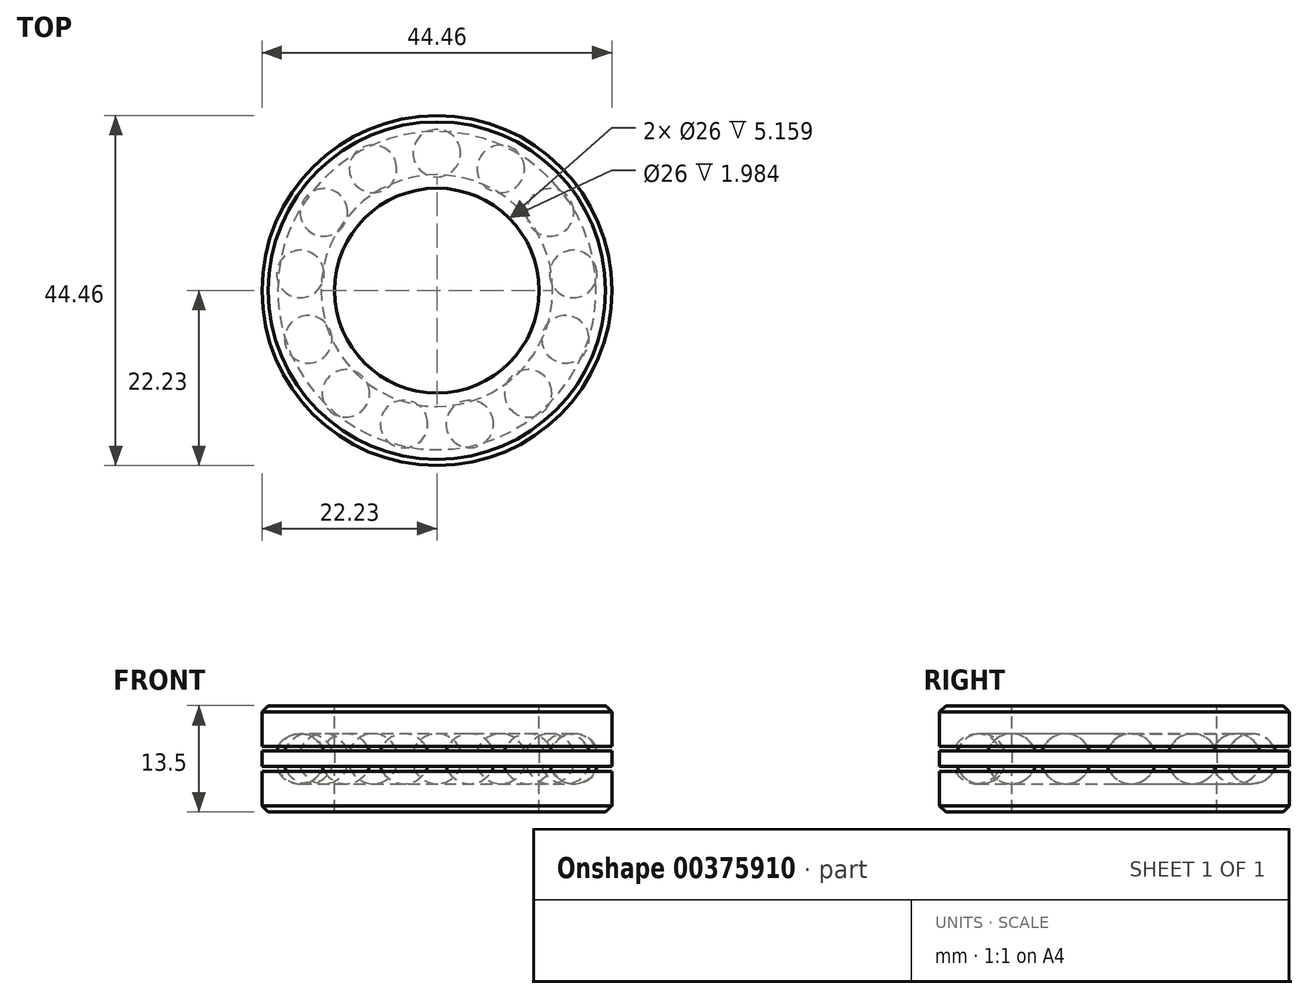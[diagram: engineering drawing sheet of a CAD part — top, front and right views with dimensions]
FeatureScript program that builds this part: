
annotation { "Feature Type Name" : "Feature", "Feature Type Description" : "" }
export const myFeature = defineFeature(function(context is Context, id is Id, definition is map)
    precondition{}
    {
        {
            var Q0;
            Q0=qCreatedBy(makeId("Top.planeOp"),FACE);
            var sketch = newSketch(context, id + "F0", { "sketchPlane" : qUnion([Q0]), "disableImprinting" : false});
            skCircle(sketch, "E0", {"center": v(0, 0) * mm, "radius": 17.46 * mm, "construction": true});
            skLineSegment(sketch, "E1", {"start": v(0, 0) * mm, "end": v(0, 34.15) * mm, "construction": true});
            skArc(sketch, "E2", {"start": v(0, 20.64) * mm, "mid": v(-3.17, 17.46) * mm, "end": v(0, 14.29) * mm});
            skLineSegment(sketch, "E3", {"start": v(0, 14.29) * mm, "end": v(0, 20.64) * mm});
            skCircle(sketch, "E4", {"center": v(0, 0) * mm, "radius": 13 * mm});
            skCircle(sketch, "E5", {"center": v(0, 0) * mm, "radius": 22.23 * mm});
            skSolve(sketch);
        }
        {
            var Q0;
            Q0=makeQuery(id+"F0.imprint","IMPRINT",FACE,{"disambiguationData":[TD([[makeQuery(id+"F0.imprint","IMPRINT",EDGE,{"derivedFrom":sQuery(id+"F0.wireOp",EDGE,"E2")}),1.0]])]});
            var Q1;
            Q1=sQuery(id+"F0.wireOp",EDGE,"E1");
            revolve(context, id + "F1", {"entities" : qUnion([Q0]), "axis" : qUnion([Q1]), "revolveType" : RevolveType.FULL});
        }
        {
            var Q0;
            Q0=makeQuery(id+"F0.imprint","IMPRINT",FACE,{"disambiguationData":[TD([[makeQuery(id+"F0.imprint","IMPRINT",EDGE,{"derivedFrom":sQuery(id+"F0.wireOp",EDGE,"E2")}),-1.0]])]});
            var Q1;
            Q1=makeQuery(id+"F0.imprint","IMPRINT",FACE,{"disambiguationData":[TD([[makeQuery(id+"F0.imprint","IMPRINT",EDGE,{"derivedFrom":sQuery(id+"F0.wireOp",EDGE,"E2")}),1.0]])]});
            extrude(context, id + "F2", {"entities" : qUnion([Q0, Q1]), "depth" : 1.98 * mm, "offsetDistance" : 25.4 * mm, "symmetric" : true});
        }
        {
            var Q0;
            Q0=makeQuery(id+"F1.opRevolve","SWEPT_BODY",BODY,{"disambiguationData":[OSD([sQuery(id+"F0.wireOp",EDGE,"E2"),sQuery(id+"F0.wireOp",EDGE,"E3")])]});
            var Q1;
            Q1=sQuery(id+"F0.wireOp",EDGE,"E0");
            circularPattern(context, id + "F3", {"entities" : qUnion([Q0]), "axis" : qUnion([Q1]), "angle" : 360 * degree, "instanceCount" : 13, "equalSpace" : true, "computeTransformsWithoutBuiltin" : true});
        }
        {
            var Q0;
            Q0=makeQuery(id+"F3.opPattern","COPY",BODY,{"derivedFrom":makeQuery(id+"F1.opRevolve","SWEPT_BODY",BODY,{"disambiguationData":[OSD([sQuery(id+"F0.wireOp",EDGE,"E2"),sQuery(id+"F0.wireOp",EDGE,"E3")])]}),"instanceName":"1"});
            var Q1;
            Q1=makeQuery(id+"F2.opExtrude","SWEPT_BODY",BODY,{"disambiguationData":[OSD([sQuery(id+"F0.wireOp",EDGE,"E4"),sQuery(id+"F0.wireOp",EDGE,"E5")])]});
            var Q2;
            Q2=makeQuery(id+"F1.opRevolve","SWEPT_BODY",BODY,{"disambiguationData":[OSD([sQuery(id+"F0.wireOp",EDGE,"E2"),sQuery(id+"F0.wireOp",EDGE,"E3")])]});
            var Q3;
            Q3=makeQuery(id+"F3.opPattern","COPY",BODY,{"derivedFrom":makeQuery(id+"F1.opRevolve","SWEPT_BODY",BODY,{"disambiguationData":[OSD([sQuery(id+"F0.wireOp",EDGE,"E2"),sQuery(id+"F0.wireOp",EDGE,"E3")])]}),"instanceName":"3"});
            var Q4;
            Q4=makeQuery(id+"F3.opPattern","COPY",BODY,{"derivedFrom":makeQuery(id+"F1.opRevolve","SWEPT_BODY",BODY,{"disambiguationData":[OSD([sQuery(id+"F0.wireOp",EDGE,"E2"),sQuery(id+"F0.wireOp",EDGE,"E3")])]}),"instanceName":"4"});
            var Q5;
            Q5=makeQuery(id+"F3.opPattern","COPY",BODY,{"derivedFrom":makeQuery(id+"F1.opRevolve","SWEPT_BODY",BODY,{"disambiguationData":[OSD([sQuery(id+"F0.wireOp",EDGE,"E2"),sQuery(id+"F0.wireOp",EDGE,"E3")])]}),"instanceName":"2"});
            var Q6;
            Q6=makeQuery(id+"F3.opPattern","COPY",BODY,{"derivedFrom":makeQuery(id+"F1.opRevolve","SWEPT_BODY",BODY,{"disambiguationData":[OSD([sQuery(id+"F0.wireOp",EDGE,"E2"),sQuery(id+"F0.wireOp",EDGE,"E3")])]}),"instanceName":"5"});
            var Q7;
            Q7=makeQuery(id+"F3.opPattern","COPY",BODY,{"derivedFrom":makeQuery(id+"F1.opRevolve","SWEPT_BODY",BODY,{"disambiguationData":[OSD([sQuery(id+"F0.wireOp",EDGE,"E2"),sQuery(id+"F0.wireOp",EDGE,"E3")])]}),"instanceName":"6"});
            var Q8;
            Q8=makeQuery(id+"F3.opPattern","COPY",BODY,{"derivedFrom":makeQuery(id+"F1.opRevolve","SWEPT_BODY",BODY,{"disambiguationData":[OSD([sQuery(id+"F0.wireOp",EDGE,"E2"),sQuery(id+"F0.wireOp",EDGE,"E3")])]}),"instanceName":"7"});
            var Q9;
            Q9=makeQuery(id+"F3.opPattern","COPY",BODY,{"derivedFrom":makeQuery(id+"F1.opRevolve","SWEPT_BODY",BODY,{"disambiguationData":[OSD([sQuery(id+"F0.wireOp",EDGE,"E2"),sQuery(id+"F0.wireOp",EDGE,"E3")])]}),"instanceName":"8"});
            var Q10;
            Q10=makeQuery(id+"F3.opPattern","COPY",BODY,{"derivedFrom":makeQuery(id+"F1.opRevolve","SWEPT_BODY",BODY,{"disambiguationData":[OSD([sQuery(id+"F0.wireOp",EDGE,"E2"),sQuery(id+"F0.wireOp",EDGE,"E3")])]}),"instanceName":"9"});
            var Q11;
            Q11=makeQuery(id+"F3.opPattern","COPY",BODY,{"derivedFrom":makeQuery(id+"F1.opRevolve","SWEPT_BODY",BODY,{"disambiguationData":[OSD([sQuery(id+"F0.wireOp",EDGE,"E2"),sQuery(id+"F0.wireOp",EDGE,"E3")])]}),"instanceName":"10"});
            var Q12;
            Q12=makeQuery(id+"F3.opPattern","COPY",BODY,{"derivedFrom":makeQuery(id+"F1.opRevolve","SWEPT_BODY",BODY,{"disambiguationData":[OSD([sQuery(id+"F0.wireOp",EDGE,"E2"),sQuery(id+"F0.wireOp",EDGE,"E3")])]}),"instanceName":"11"});
            var Q13;
            Q13=makeQuery(id+"F3.opPattern","COPY",BODY,{"derivedFrom":makeQuery(id+"F1.opRevolve","SWEPT_BODY",BODY,{"disambiguationData":[OSD([sQuery(id+"F0.wireOp",EDGE,"E2"),sQuery(id+"F0.wireOp",EDGE,"E3")])]}),"instanceName":"12"});
            booleanBodies(context, id + "F4", {"operationType" : BooleanOperationType.UNION, "tools" : qUnion([Q0, Q1, Q2, Q3, Q4, Q5, Q6, Q7, Q8, Q9, Q10, Q11, Q12, Q13])});
        }
        {
            var Q0;
            Q0=qCreatedBy(makeId("Right.planeOp"),FACE);
            var sketch = newSketch(context, id + "F5", { "sketchPlane" : qUnion([Q0])});
            skArc(sketch, "E6", {"start": v(14.45, 1) * mm, "mid": v(17.46, 3.18) * mm, "end": v(20.48, 1) * mm});
            skArc(sketch, "E7", {"start": v(20.48, -1) * mm, "mid": v(17.46, -3.18) * mm, "end": v(14.45, -1) * mm});
            skLineSegment(sketch, "E8.0", {"start": v(-13, 0) * mm, "end": v(13, 0) * mm});
            skLineSegment(sketch, "E9.0", {"start": v(-22.23, 0) * mm, "end": v(22.23, 0) * mm});
            skLineSegment(sketch, "E10.0.0", {"start": v(-13, 0) * mm, "end": v(13, 0) * mm, "construction": true});
            skLineSegment(sketch, "E11", {"start": v(22.23, 0) * mm, "end": v(22.23, 13.5) * mm, "construction": true});
            skLineSegment(sketch, "E12", {"start": v(22.23, 13.5) * mm, "end": v(22.23, -14.55) * mm, "construction": true});
            skLineSegment(sketch, "E13", {"start": v(22.6, 1.59) * mm, "end": v(20.21, 1.59) * mm, "construction": true});
            skLineSegment(sketch, "E14", {"start": v(22.73, 6.75) * mm, "end": v(-0.67, 6.75) * mm, "construction": true});
            skPoint(sketch, "E14.startSnap0", {"position": v(22.23, 6.75) * mm});
            skLineSegment(sketch, "E15", {"start": v(13, 0) * mm, "end": v(13, 10.3) * mm, "construction": true});
            skLineSegment(sketch, "E16.bottom", {"start": v(13, 1.59) * mm, "end": v(14.71, 1.59) * mm});
            skLineSegment(sketch, "E16.top", {"start": v(13, 6.75) * mm, "end": v(22.23, 6.75) * mm});
            skLineSegment(sketch, "E16.left", {"start": v(13, 1.59) * mm, "end": v(13, 6.75) * mm});
            skLineSegment(sketch, "E16.right", {"start": v(22.23, 1.59) * mm, "end": v(22.23, 6.75) * mm});
            skLineSegment(sketch, "E17.MirrorCS", {"start": v(22.73, -6.75) * mm, "end": v(-0.67, -6.75) * mm, "construction": true});
            skLineSegment(sketch, "E18.MirrorCS", {"start": v(22.6, -1.59) * mm, "end": v(20.21, -1.59) * mm, "construction": true});
            skLineSegment(sketch, "E19.MirrorCS", {"start": v(13, 0) * mm, "end": v(13, -10.3) * mm, "construction": true});
            skLineSegment(sketch, "E20.bottom", {"start": v(13, -1.59) * mm, "end": v(14.71, -1.59) * mm});
            skLineSegment(sketch, "E20.top", {"start": v(13, -6.75) * mm, "end": v(22.23, -6.75) * mm});
            skLineSegment(sketch, "E20.left", {"start": v(13, -1.59) * mm, "end": v(13, -6.75) * mm});
            skLineSegment(sketch, "E20.right", {"start": v(22.23, -1.59) * mm, "end": v(22.23, -6.75) * mm});
            skLineSegment(sketch, "E21.trimOffspring", {"start": v(14.71, -1.59) * mm, "end": v(-2.74, -1.59) * mm, "construction": true});
            skLineSegment(sketch, "E22.trimOffspring", {"start": v(14.71, 1.59) * mm, "end": v(-2.74, 1.59) * mm, "construction": true});
            skLineSegment(sketch, "E23.trimOffspring", {"start": v(20.21, 1.59) * mm, "end": v(22.23, 1.59) * mm});
            skLineSegment(sketch, "E24.trimOffspring", {"start": v(20.21, -1.59) * mm, "end": v(22.23, -1.59) * mm});
            skLineSegment(sketch, "E25", {"start": v(0, 0) * mm, "end": v(0, -11.38) * mm, "construction": true});
            skSolve(sketch);
        }
        {
            var Q0;
            {var subQ0=sQuery(id+"F5.wireOp",EDGE,"E20.bottom");Q0=makeQuery(id+"F5.imprint","IMPRINT",FACE,{"disambiguationData":[TD([[makeQuery(id+"F5.imprint","IMPRINT",EDGE,{"derivedFrom":subQ0}),-1.0]])]});}
            var Q1;
            {var subQ0=sQuery(id+"F5.wireOp",EDGE,"E16.bottom");Q1=makeQuery(id+"F5.imprint","IMPRINT",FACE,{"disambiguationData":[TD([[makeQuery(id+"F5.imprint","IMPRINT",EDGE,{"derivedFrom":subQ0}),1.0]])]});}
            var Q2;
            Q2=sQuery(id+"F5.wireOp",EDGE,"E25");
            revolve(context, id + "F6", {"operationType" : NewBodyOperationType.ADD, "entities" : qUnion([Q0, Q1]), "axis" : qUnion([Q2]), "revolveType" : RevolveType.FULL});
        }
        {
            var Q0;
            Q0=makeQuery(id+"F6.opRevolve","SWEPT_EDGE",EDGE,{"disambiguationData":[OSD([sQuery(id+"F5.wireOp",EDGE,"E20.top"),sQuery(id+"F5.wireOp",EDGE,"E20.right")])]});
            var Q1;
            Q1=makeQuery(id+"F6.opRevolve","SWEPT_EDGE",EDGE,{"disambiguationData":[OSD([sQuery(id+"F5.wireOp",EDGE,"E16.top"),sQuery(id+"F5.wireOp",EDGE,"E16.right")])]});
            chamfer(context, id + "F7", {"entities" : qUnion([Q0, Q1]), "width" : 0.8 * mm, "tangentPropagation" : true});
        }
    });
